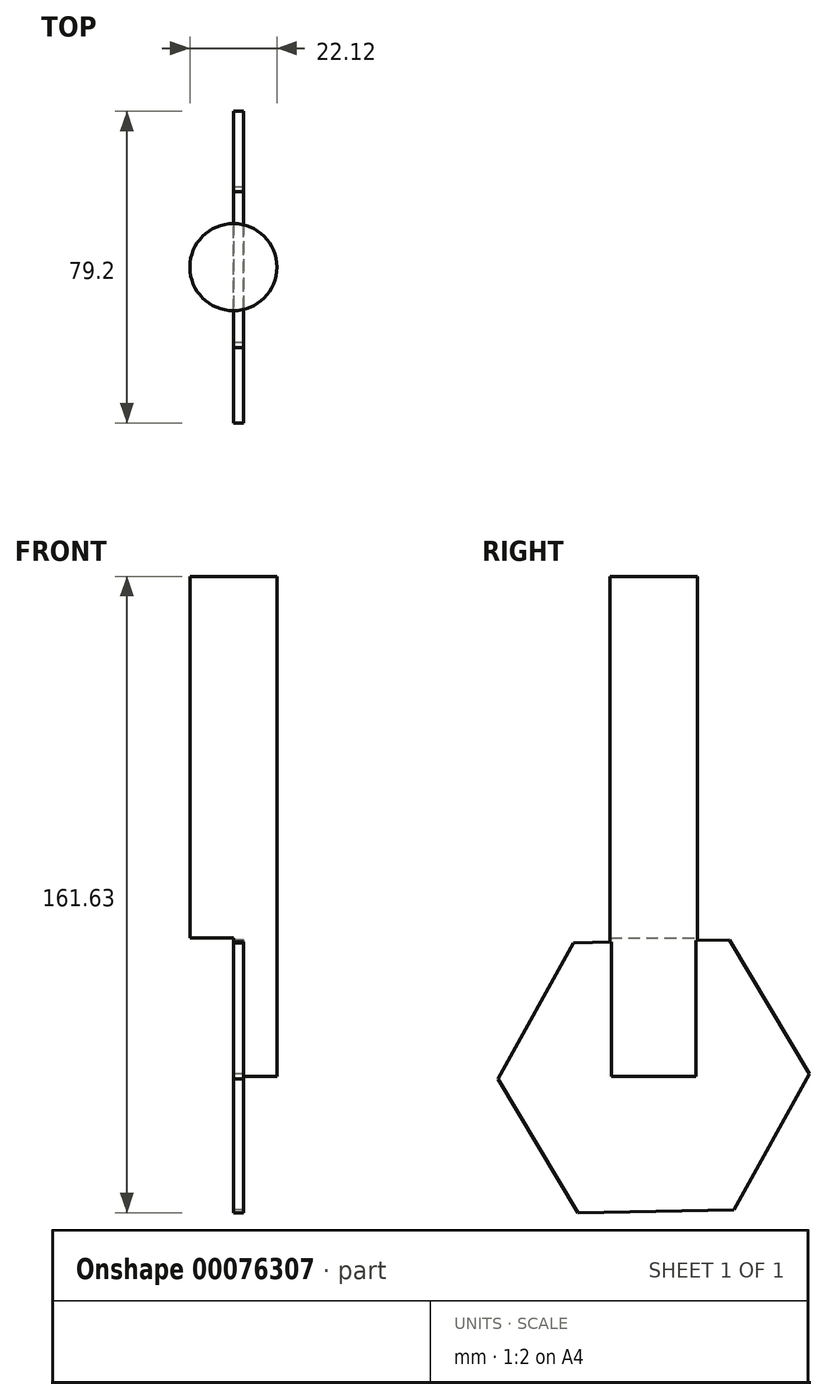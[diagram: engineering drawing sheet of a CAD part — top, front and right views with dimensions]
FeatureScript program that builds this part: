
annotation { "Feature Type Name" : "Feature", "Feature Type Description" : "" }
export const myFeature = defineFeature(function(context is Context, id is Id, definition is map)
    precondition{}
    {
        {
            var Q0;
            Q0=qCreatedBy(makeId("Top.planeOp"),FACE);
            var sketch = newSketch(context, id + "F0", { "sketchPlane" : qUnion([Q0])});
            skCircle(sketch, "E0", {"center": v(0, 0) * mm, "radius": 11.06 * mm});
            skSolve(sketch);
        }
        {
            var Q0;
            Q0=makeQuery(id+"F0.imprint","IMPRINT",FACE,{"disambiguationData":[TD([[makeQuery(id+"F0.imprint","IMPRINT",EDGE,{"derivedFrom":sQuery(id+"F0.wireOp",EDGE,"E0")}),1.0]])]});
            extrude(context, id + "F1", {"entities" : qUnion([Q0]), "depth" : 127 * mm});
        }
        {
            var Q0;
            Q0=qCreatedBy(makeId("Right.planeOp"),FACE);
            var sketch = newSketch(context, id + "F2", { "sketchPlane" : qUnion([Q0])});
            skCircle(sketch, "E1.cCircle", {"center": v(0, 0) * mm, "radius": 34.3 * mm, "construction": true});
            skLineSegment(sketch, "E1.0", {"start": v(39.6, 0.67) * mm, "end": v(20.38, -33.96) * mm});
            skLineSegment(sketch, "E1.1", {"start": v(20.38, -33.96) * mm, "end": v(-19.22, -34.63) * mm});
            skLineSegment(sketch, "E1.2", {"start": v(-19.22, -34.63) * mm, "end": v(-39.6, -0.67) * mm});
            skLineSegment(sketch, "E1.3", {"start": v(-39.6, -0.67) * mm, "end": v(-20.38, 33.96) * mm});
            skLineSegment(sketch, "E1.4", {"start": v(-20.38, 33.96) * mm, "end": v(19.22, 34.63) * mm});
            skLineSegment(sketch, "E1.5", {"start": v(19.22, 34.63) * mm, "end": v(39.6, 0.67) * mm});
            skPoint(sketch, "E1.0.midPoint", {"position": v(30, -16.64) * mm});
            skSolve(sketch);
        }
        {
            var Q0;
            Q0=makeQuery(id+"F2.imprint","IMPRINT",FACE,{"disambiguationData":[TD([[makeQuery(id+"F2.imprint","IMPRINT",EDGE,{"derivedFrom":sQuery(id+"F2.wireOp",EDGE,"E1.0")}),-1.0]])]});
            extrude(context, id + "F3", {"entities" : qUnion([Q0]), "operationType" : NewBodyOperationType.ADD, "depth" : 2.54 * mm});
        }
        {
            var Q0;
            Q0=qCreatedBy(makeId("Front.planeOp"),FACE);
            var sketch = newSketch(context, id + "F4", { "sketchPlane" : qUnion([Q0])});
            skLineSegment(sketch, "E2.bottom", {"start": v(0, 35.16) * mm, "end": v(-12.08, 35.16) * mm});
            skLineSegment(sketch, "E2.top", {"start": v(0, 0) * mm, "end": v(-12.08, 0) * mm});
            skLineSegment(sketch, "E2.left", {"start": v(0, 35.16) * mm, "end": v(0, 0) * mm});
            skLineSegment(sketch, "E2.right", {"start": v(-12.08, 35.16) * mm, "end": v(-12.08, 0) * mm});
            skSolve(sketch);
        }
        {
            var Q0;
            Q0=makeQuery(id+"F4.imprint","IMPRINT",FACE,{"disambiguationData":[TD([[makeQuery(id+"F4.imprint","IMPRINT",EDGE,{"derivedFrom":sQuery(id+"F4.wireOp",EDGE,"E2.bottom")}),1.0]])]});
            extrude(context, id + "F5", {"entities" : qUnion([Q0]), "operationType" : NewBodyOperationType.REMOVE, "endBound" : BoundingType.THROUGH_ALL, "depth" : 25.4 * mm, "hasSecondDirection" : true, "secondDirectionOppositeDirection" : true, "secondDirectionDepth" : 25.4 * mm});
        }
    });
